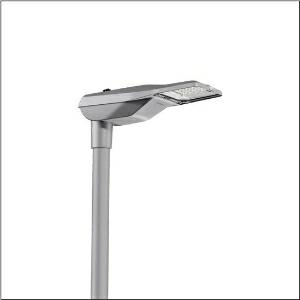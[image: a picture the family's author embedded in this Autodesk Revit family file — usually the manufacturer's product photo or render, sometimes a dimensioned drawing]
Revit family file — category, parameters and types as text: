
# Revit family: streetlight_sl_21_micro___pl52_5xe1h33s08db_2be5
name_source: partatom
category: Lighting Fixtures
units: mm (PartAtom-declared; Revit-internal decimal feet)

## family parameters
Cut with Voids When Loaded = No
Host = Face
Light Source = No
Part Type = Normal
Room Calculation Point = No
Round Connector Dimension = Use Diameter
Shared = No

## types (1)
- --- (1 x LED, 5020 lm, 39.1 W, 3000K)
    Apparent Load = 39 VA
    CIE Flux Codes = 27 59 98 100 100
    Color Rendering = 70
    Color Temperature = 3000K
    Default Elevation = 1800 mm
    Description = Streetlight SL 21 micro, mast luminaire, primary light control with lens, of PMMA, primary optical cover: cover, of toughened safety glass, transparent, light distribution: PL52, light emission: direct distribution, primary light characteristic: asymmetric, installation type: side-entry, post-top, LED, High Power LED, rated luminous flux: 5.020lm, luminous efficacy: 128lm/W, light colour: 730, colour temperature: 3000K, control gear: D4i, control: flexible luminous flux parameterisation, time-dependent luminous flux control, constant luminous flux control, overheat protection, pre-setting: logarithmic dimming characteristic, mains connection: 220..240V, AC, 50/60Hz, start of lifetime: 39W, end of service life: 41W, reduction: 18W, luminaire housing, of diecast aluminium, powder-coated, Siteco® metallic grey (DB 702S), corrosivity category C5 mid according to DIN EN ISO 12944, please order mast flange separately, inclination adjustable: 0°, 5°, 10°, 15°, sealing non-destructively replaceable, multi-level sealing system, length: 528mm, width: 235mm, height: 110mm, mast flange for spigot size: 42mm (side-entry): 5XC10008XM4, 60/48mm (side-entry/post-top): 5XC10108XM2, 76/60mm (side-entry/post-top): 5XC10108XM1, Smart Interface above, protection rating (complete): IP66, insulation class (complete): insulation class II (safety insulation), certification: CE, ENEC, ENEC+, VDE, impact resistance: IK10, permissible operating ambient temperature for outdoor applications: -40..+50°C, standard-compliant lighting for roads and squares, packaging unit: 1 piece

Light Distribution: PL52
    Height = 110 mm
    Lamp = 1 x LED
    Lamp Light Flux = 5020 lm
    Lamp Power = 39.1 W
    Lamp count = 1
    Length = 528 mm
    Luminous efficacy = 128 lm/W
    Manufacturer = Siteco
    ModVariant = No
    Model = 5XE1H33S08DB
    Number of Poles = 1
    OnlyDefault = Yes
    Power Factor = 1
    Product Name = Streetlight SL 21 micro | PL52
    Product group = mast luminaire | pylon top
    ProductGroupID = 6100
    Protection Class = Protection class II
    Protection Degree = IP 66
    RLX_Detail_Level = 1
    RLX_Emergency_Light_Flux = 0 lm
    RLX_Emergency_Type = 0
    RLX_Emergency_Type_DB = No
    RlxData = <blob elided: 107933 chars, md5=1a693610>
    Socket = socket
    Standby Power = 0 W
    System Light Flux = 5020 lm
    System Power = 39 W
    Type Comments = factory setting: luminous flux: 100 % | dim-lin: 254 | 765 mA
    Type Image = l_1277292.jpg
    URL = http://relux.com
    VarID = @adj_156288
    Voltage = 0 V
    Weight = 0.00 kg
    Width = 235 mm

## geometry (parser evidence)
native form markers: Blend x4, Sweep x10
no freeform markers — native parametric forms only
